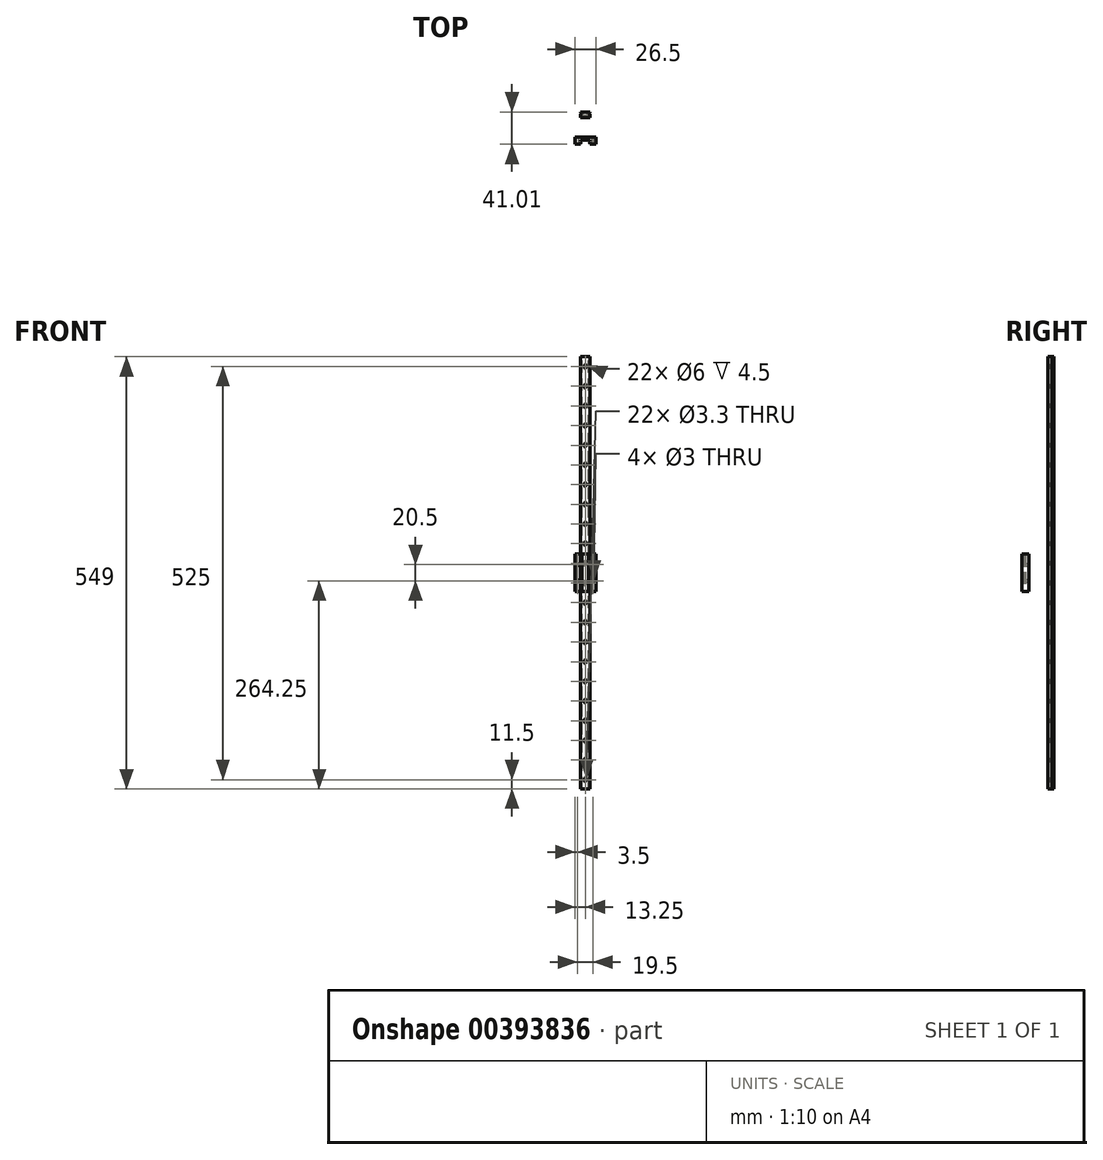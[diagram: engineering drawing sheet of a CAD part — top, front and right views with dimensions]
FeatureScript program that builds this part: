
annotation { "Feature Type Name" : "Feature", "Feature Type Description" : "" }
export const myFeature = defineFeature(function(context is Context, id is Id, definition is map)
    precondition{}
    {
        {
            var Q0;
            Q0=qCreatedBy(makeId("Front.planeOp"),FACE);
            var sketch = newSketch(context, id + "F0", { "sketchPlane" : qUnion([Q0])});
            skLineSegment(sketch, "E0.bottom", {"start": v(-6, 274.5) * mm, "end": v(6, 274.5) * mm});
            skLineSegment(sketch, "E0.top", {"start": v(-6, -274.5) * mm, "end": v(6, -274.5) * mm});
            skLineSegment(sketch, "E0.left", {"start": v(-6, 274.5) * mm, "end": v(-6, -274.5) * mm});
            skLineSegment(sketch, "E0.right", {"start": v(6, 274.5) * mm, "end": v(6, -274.5) * mm});
            skPoint(sketch, "E0.middle", {"position": v(0, 0) * mm});
            skSolve(sketch);
        }
        {
            var Q0;
            Q0=qSketchRegion(id+"F0",true);
            extrude(context, id + "F1", {"entities" : qUnion([Q0]), "endBound" : BoundingType.SYMMETRIC, "depth" : 7.4 * mm});
        }
        {
            var Q0;
            Q0=makeQuery(id+"F1.opExtrude","SWEPT_FACE",FACE,{"disambiguationData":[OSD([sQuery(id+"F0.wireOp",EDGE,"E0.bottom")])]});
            var sketch = newSketch(context, id + "F2", { "sketchPlane" : qUnion([Q0])});
            skLineSegment(sketch, "E1", {"start": v(-6, 2.7) * mm, "end": v(-4, 1.7) * mm});
            skLineSegment(sketch, "E2", {"start": v(-4, 1.7) * mm, "end": v(-6, 1.03) * mm});
            skLineSegment(sketch, "E3.MirrorCS", {"start": v(6, 2.7) * mm, "end": v(4, 1.7) * mm});
            skLineSegment(sketch, "E4.MirrorCS", {"start": v(4, 1.7) * mm, "end": v(6, 1.03) * mm});
            skSolve(sketch);
        }
        {
            var Q0;
            {var subQ0=sQuery(id+"F2.wireOp",EDGE,"E1");Q0=makeQuery(id+"F2.imprint","IMPRINT",FACE,{"disambiguationData":[TD([[makeQuery(id+"F2.imprint","IMPRINT",EDGE,{"derivedFrom":subQ0}),-1.0]])]});}
            var Q1;
            {var subQ0=sQuery(id+"F2.wireOp",EDGE,"E3.MirrorCS");Q1=makeQuery(id+"F2.imprint","IMPRINT",FACE,{"disambiguationData":[TD([[makeQuery(id+"F2.imprint","IMPRINT",EDGE,{"derivedFrom":subQ0}),1.0]])]});}
            extrude(context, id + "F3", {"entities" : qUnion([Q0, Q1]), "operationType" : NewBodyOperationType.REMOVE, "endBound" : BoundingType.THROUGH_ALL, "oppositeDirection" : true, "depth" : 100 * mm});
        }
        {
            var Q0;
            Q0=makeQuery(id+"F1.opExtrude","CAP_FACE",FACE,{"disambiguationData":[OSD([sQuery(id+"F0.wireOp",EDGE,"E0.bottom"),sQuery(id+"F0.wireOp",EDGE,"E0.top"),sQuery(id+"F0.wireOp",EDGE,"E0.left"),sQuery(id+"F0.wireOp",EDGE,"E0.right")])],"isStart":true});
            var sketch = newSketch(context, id + "F4", { "sketchPlane" : qUnion([Q0])});
            skCircle(sketch, "E5", {"center": v(0, 262) * mm, "radius": 3 * mm});
            skPoint(sketch, "E6", {"position": v(0, 274.5) * mm});
            skCircle(sketch, "E7.0.1.0", {"center": v(0, 237) * mm, "radius": 3 * mm});
            skCircle(sketch, "E7.0.2.0", {"center": v(0, 212) * mm, "radius": 3 * mm});
            skCircle(sketch, "E7.0.3.0", {"center": v(0, 187) * mm, "radius": 3 * mm});
            skCircle(sketch, "E7.0.4.0", {"center": v(0, 162) * mm, "radius": 3 * mm});
            skCircle(sketch, "E7.0.5.0", {"center": v(0, 137) * mm, "radius": 3 * mm});
            skCircle(sketch, "E7.0.6.0", {"center": v(0, 112) * mm, "radius": 3 * mm});
            skCircle(sketch, "E7.0.7.0", {"center": v(0, 87) * mm, "radius": 3 * mm});
            skCircle(sketch, "E7.0.8.0", {"center": v(0, 62) * mm, "radius": 3 * mm});
            skCircle(sketch, "E7.0.9.0", {"center": v(0, 37) * mm, "radius": 3 * mm});
            skCircle(sketch, "E7.0.10.0", {"center": v(0, 12) * mm, "radius": 3 * mm});
            skCircle(sketch, "E7.0.11.0", {"center": v(0, -13) * mm, "radius": 3 * mm});
            skCircle(sketch, "E7.0.12.0", {"center": v(0, -38) * mm, "radius": 3 * mm});
            skCircle(sketch, "E7.0.13.0", {"center": v(0, -63) * mm, "radius": 3 * mm});
            skCircle(sketch, "E7.0.14.0", {"center": v(0, -88) * mm, "radius": 3 * mm});
            skCircle(sketch, "E7.0.15.0", {"center": v(0, -113) * mm, "radius": 3 * mm});
            skCircle(sketch, "E7.0.16.0", {"center": v(0, -138) * mm, "radius": 3 * mm});
            skCircle(sketch, "E7.0.17.0", {"center": v(0, -163) * mm, "radius": 3 * mm});
            skCircle(sketch, "E7.0.18.0", {"center": v(0, -188) * mm, "radius": 3 * mm});
            skCircle(sketch, "E7.0.19.0", {"center": v(0, -213) * mm, "radius": 3 * mm});
            skCircle(sketch, "E7.0.20.0", {"center": v(0, -238) * mm, "radius": 3 * mm});
            skCircle(sketch, "E7.0.21.0", {"center": v(0, -263) * mm, "radius": 3 * mm});
            skLineSegment(sketch, "E7.direction1", {"start": v(0, 262) * mm, "end": v(25, 262) * mm, "construction": true});
            skLineSegment(sketch, "E7.direction2", {"start": v(0, 262) * mm, "end": v(0, 237) * mm, "construction": true});
            skSolve(sketch);
        }
        {
            var Q0;
            Q0=qSketchRegion(id+"F4",true);
            extrude(context, id + "F5", {"entities" : qUnion([Q0]), "operationType" : NewBodyOperationType.REMOVE, "oppositeDirection" : true, "depth" : 4.5 * mm});
        }
        {
            var Q0;
            Q0=makeQuery(id+"F1.opExtrude","CAP_FACE",FACE,{"disambiguationData":[OSD([sQuery(id+"F0.wireOp",EDGE,"E0.bottom"),sQuery(id+"F0.wireOp",EDGE,"E0.top"),sQuery(id+"F0.wireOp",EDGE,"E0.left"),sQuery(id+"F0.wireOp",EDGE,"E0.right")])],"isStart":false});
            var sketch = newSketch(context, id + "F6", { "sketchPlane" : qUnion([Q0])});
            skCircle(sketch, "E8", {"center": v(0, 262) * mm, "radius": 1.65 * mm});
            skCircle(sketch, "E9.0.1.0", {"center": v(0, 237) * mm, "radius": 1.65 * mm});
            skCircle(sketch, "E9.0.2.0", {"center": v(0, 212) * mm, "radius": 1.65 * mm});
            skCircle(sketch, "E9.0.3.0", {"center": v(0, 187) * mm, "radius": 1.65 * mm});
            skCircle(sketch, "E9.0.4.0", {"center": v(0, 162) * mm, "radius": 1.65 * mm});
            skCircle(sketch, "E9.0.5.0", {"center": v(0, 137) * mm, "radius": 1.65 * mm});
            skCircle(sketch, "E9.0.6.0", {"center": v(0, 112) * mm, "radius": 1.65 * mm});
            skCircle(sketch, "E9.0.7.0", {"center": v(0, 87) * mm, "radius": 1.65 * mm});
            skCircle(sketch, "E9.0.8.0", {"center": v(0, 62) * mm, "radius": 1.65 * mm});
            skCircle(sketch, "E9.0.9.0", {"center": v(0, 37) * mm, "radius": 1.65 * mm});
            skCircle(sketch, "E9.0.10.0", {"center": v(0, 12) * mm, "radius": 1.65 * mm});
            skCircle(sketch, "E9.0.11.0", {"center": v(0, -13) * mm, "radius": 1.65 * mm});
            skCircle(sketch, "E9.0.12.0", {"center": v(0, -38) * mm, "radius": 1.65 * mm});
            skCircle(sketch, "E9.0.13.0", {"center": v(0, -63) * mm, "radius": 1.65 * mm});
            skCircle(sketch, "E9.0.14.0", {"center": v(0, -88) * mm, "radius": 1.65 * mm});
            skCircle(sketch, "E9.0.15.0", {"center": v(0, -113) * mm, "radius": 1.65 * mm});
            skCircle(sketch, "E9.0.16.0", {"center": v(0, -138) * mm, "radius": 1.65 * mm});
            skCircle(sketch, "E9.0.17.0", {"center": v(0, -163) * mm, "radius": 1.65 * mm});
            skCircle(sketch, "E9.0.18.0", {"center": v(0, -188) * mm, "radius": 1.65 * mm});
            skCircle(sketch, "E9.0.19.0", {"center": v(0, -213) * mm, "radius": 1.65 * mm});
            skCircle(sketch, "E9.0.20.0", {"center": v(0, -238) * mm, "radius": 1.65 * mm});
            skCircle(sketch, "E9.0.21.0", {"center": v(0, -263) * mm, "radius": 1.65 * mm});
            skLineSegment(sketch, "E9.direction1", {"start": v(0, 262) * mm, "end": v(25, 262) * mm, "construction": true});
            skLineSegment(sketch, "E9.direction2", {"start": v(0, 262) * mm, "end": v(0, 237) * mm, "construction": true});
            skSolve(sketch);
        }
        {
            var Q0;
            Q0=qSketchRegion(id+"F6",true);
            extrude(context, id + "F7", {"entities" : qUnion([Q0]), "operationType" : NewBodyOperationType.REMOVE, "oppositeDirection" : true, "depth" : 25 * mm});
        }
        {
            var Q0;
            Q0=qCreatedBy(makeId("Top.planeOp"),FACE);
            var sketch = newSketch(context, id + "F8", { "sketchPlane" : qUnion([Q0])});
            skLineSegment(sketch, "E10.bottom", {"start": v(-13.25, -28.3) * mm, "end": v(13.25, -28.3) * mm});
            skLineSegment(sketch, "E10.top", {"start": v(-13.25, -37.3) * mm, "end": v(-6, -37.3) * mm});
            skLineSegment(sketch, "E10.left", {"start": v(-13.25, -28.3) * mm, "end": v(-13.25, -37.3) * mm});
            skLineSegment(sketch, "E10.right", {"start": v(13.25, -28.3) * mm, "end": v(13.25, -37.3) * mm});
            skLineSegment(sketch, "E11.bottom", {"start": v(-6, -32.3) * mm, "end": v(6, -32.3) * mm});
            skLineSegment(sketch, "E12", {"start": v(-6, -33.3) * mm, "end": v(-4.16, -34.3) * mm});
            skLineSegment(sketch, "E13", {"start": v(-4.16, -34.3) * mm, "end": v(-6, -34.85) * mm});
            skLineSegment(sketch, "E14", {"start": v(-6, -32.3) * mm, "end": v(-6, -33.3) * mm});
            skLineSegment(sketch, "E15", {"start": v(-6, -34.85) * mm, "end": v(-6, -37.3) * mm});
            skLineSegment(sketch, "E16.MirrorCS", {"start": v(6, -33.3) * mm, "end": v(4.16, -34.3) * mm});
            skLineSegment(sketch, "E17.MirrorCS", {"start": v(4.16, -34.3) * mm, "end": v(6, -34.85) * mm});
            skLineSegment(sketch, "E18", {"start": v(6, -33.3) * mm, "end": v(6, -32.3) * mm});
            skLineSegment(sketch, "E19", {"start": v(6, -34.85) * mm, "end": v(6, -37.3) * mm});
            skLineSegment(sketch, "E20.trimOffspring", {"start": v(6, -37.3) * mm, "end": v(13.25, -37.3) * mm});
            skSolve(sketch);
        }
        {
            var Q0;
            Q0=makeQuery(id+"F8.imprint","IMPRINT",FACE,{"disambiguationData":[TD([[makeQuery(id+"F8.imprint","IMPRINT",EDGE,{"derivedFrom":sQuery(id+"F8.wireOp",EDGE,"E10.bottom")}),-1.0]])]});
            extrude(context, id + "F9", {"entities" : qUnion([Q0]), "endBound" : BoundingType.SYMMETRIC, "depth" : 47.5 * mm});
        }
        {
            var Q0;
            Q0=makeQuery(id+"F9.opExtrude","SWEPT_FACE",FACE,{"disambiguationData":[OSD([sQuery(id+"F8.wireOp",EDGE,"E10.bottom")])]});
            var sketch = newSketch(context, id + "F10", { "sketchPlane" : qUnion([Q0])});
            skCircle(sketch, "E21", {"center": v(9.75, -10.25) * mm, "radius": 1.5 * mm});
            skCircle(sketch, "E22.MirrorC", {"center": v(9.75, 10.25) * mm, "radius": 1.5 * mm});
            skCircle(sketch, "E23.MirrorC", {"center": v(-9.75, 10.25) * mm, "radius": 1.5 * mm});
            skCircle(sketch, "E24.MirrorC", {"center": v(-9.75, -10.25) * mm, "radius": 1.5 * mm});
            skSolve(sketch);
        }
        {
            var Q0;
            Q0=qSketchRegion(id+"F10",true);
            extrude(context, id + "F11", {"entities" : qUnion([Q0]), "operationType" : NewBodyOperationType.REMOVE, "oppositeDirection" : true, "depth" : 25 * mm});
        }
    });
